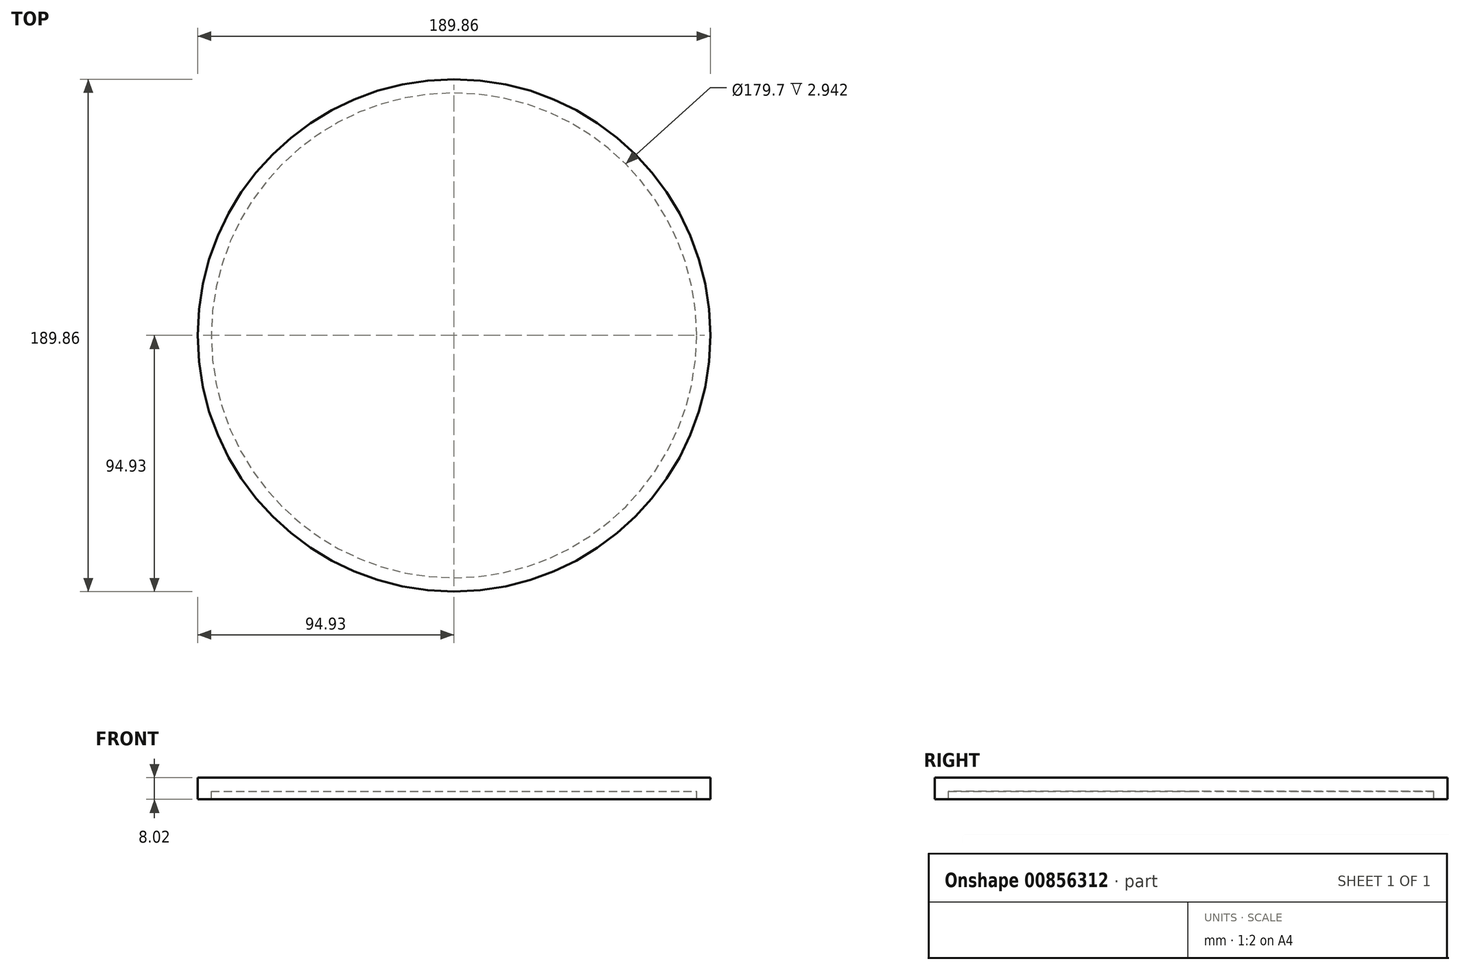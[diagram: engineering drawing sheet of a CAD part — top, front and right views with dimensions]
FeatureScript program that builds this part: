
annotation { "Feature Type Name" : "Feature", "Feature Type Description" : "" }
export const myFeature = defineFeature(function(context is Context, id is Id, definition is map)
    precondition{}
    {
        {
            var Q0;
            Q0=qCreatedBy(makeId("Right.planeOp"),FACE);
            var sketch = newSketch(context, id + "F0", { "sketchPlane" : qUnion([Q0])});
            skLineSegment(sketch, "E0", {"start": v(0, 110.06) * mm, "end": v(0, -86.77) * mm});
            skSolve(sketch);
        }
        {
            var Q0;
            Q0=qCreatedBy(makeId("Right.planeOp"),FACE);
            var sketch = newSketch(context, id + "F1", { "sketchPlane" : qUnion([Q0])});
            skLineSegment(sketch, "E1", {"start": v(0, 20.74) * mm, "end": v(-102.5, 3.63) * mm});
            skLineSegment(sketch, "E2", {"start": v(-102.5, 3.63) * mm, "end": v(0, 0) * mm});
            skSolve(sketch);
        }
        {
            var Q0;
            Q0=sQuery(id+"F1.wireOp",EDGE,"E1");
            var Q1;
            Q1=sQuery(id+"F1.wireOp",EDGE,"E2");
            var Q2;
            Q2=sQuery(id+"F0.wireOp",EDGE,"E0");
            revolve(context, id + "F2", {"bodyType" : ToolBodyType.SURFACE, "surfaceOperationType" : NewSurfaceOperationType.NEW, "surfaceEntities" : qUnion([Q0, Q1]), "axis" : qUnion([Q2]), "revolveType" : RevolveType.FULL});
        }
        {
            var Q0;
            Q0=qCreatedBy(makeId("Right.planeOp"),FACE);
            var sketch = newSketch(context, id + "F3", { "sketchPlane" : qUnion([Q0])});
            skArc(sketch, "E3", {"start": v(0, 39.84) * mm, "mid": v(-11.33, 31.17) * mm, "end": v(-5.92, 17.97) * mm});
            skSolve(sketch);
        }
        {
            var Q0;
            Q0=qCreatedBy(makeId("Right.planeOp"),FACE);
            var sketch = newSketch(context, id + "F4", { "sketchPlane" : qUnion([Q0])});
            skLineSegment(sketch, "E4.bottom", {"start": v(-94.93, 3.16) * mm, "end": v(0, 3.16) * mm});
            skLineSegment(sketch, "E4.top", {"start": v(-94.93, -4.86) * mm, "end": v(0, -4.86) * mm});
            skLineSegment(sketch, "E4.left", {"start": v(-94.93, 3.16) * mm, "end": v(-94.93, -4.86) * mm});
            skLineSegment(sketch, "E4.right", {"start": v(0, 3.16) * mm, "end": v(0, -4.86) * mm});
            skSolve(sketch);
        }
        {
            var Q0;
            Q0=qCreatedBy(makeId("Right.planeOp"),FACE);
            var sketch = newSketch(context, id + "F5", { "sketchPlane" : qUnion([Q0])});
            skLineSegment(sketch, "E5", {"start": v(0, 0) * mm, "end": v(0, -37.43) * mm});
            skSolve(sketch);
        }
        {
            var Q0;
            Q0=makeQuery(id+"F4.imprint","IMPRINT",FACE,{"disambiguationData":[TD([[makeQuery(id+"F4.imprint","IMPRINT",EDGE,{"derivedFrom":sQuery(id+"F4.wireOp",EDGE,"E4.bottom")}),-1.0]])]});
            var Q1;
            Q1=sQuery(id+"F5.wireOp",EDGE,"E5");
            revolve(context, id + "F6", {"surfaceOperationType" : NewSurfaceOperationType.NEW, "entities" : qUnion([Q0]), "axis" : qUnion([Q1]), "revolveType" : RevolveType.FULL});
        }
        {
            var Q0;
            Q0=makeQuery(id+"F6.opRevolve","SWEPT_FACE",FACE,{"disambiguationData":[OSD([sQuery(id+"F4.wireOp",EDGE,"E4.top")])]});
            shell(context, id + "F7", {"entities" : qUnion([Q0]), "thickness" : 5.08 * mm});
        }
        {
            var Q0;
            Q0=qCreatedBy(makeId("Right.planeOp"),FACE);
            var sketch = newSketch(context, id + "F8", { "sketchPlane" : qUnion([Q0])});
            skLineSegment(sketch, "E6", {"start": v(0, 50.22) * mm, "end": v(0, -32.6) * mm});
            skSolve(sketch);
        }
        {
            var Q0;
            Q0=sQuery(id+"F3.wireOp",EDGE,"E3");
            var Q1;
            Q1=sQuery(id+"F8.wireOp",EDGE,"E6");
            revolve(context, id + "F9", {"bodyType" : ToolBodyType.SURFACE, "surfaceOperationType" : NewSurfaceOperationType.NEW, "surfaceEntities" : qUnion([Q0]), "axis" : qUnion([Q1]), "revolveType" : RevolveType.FULL});
        }
    });
